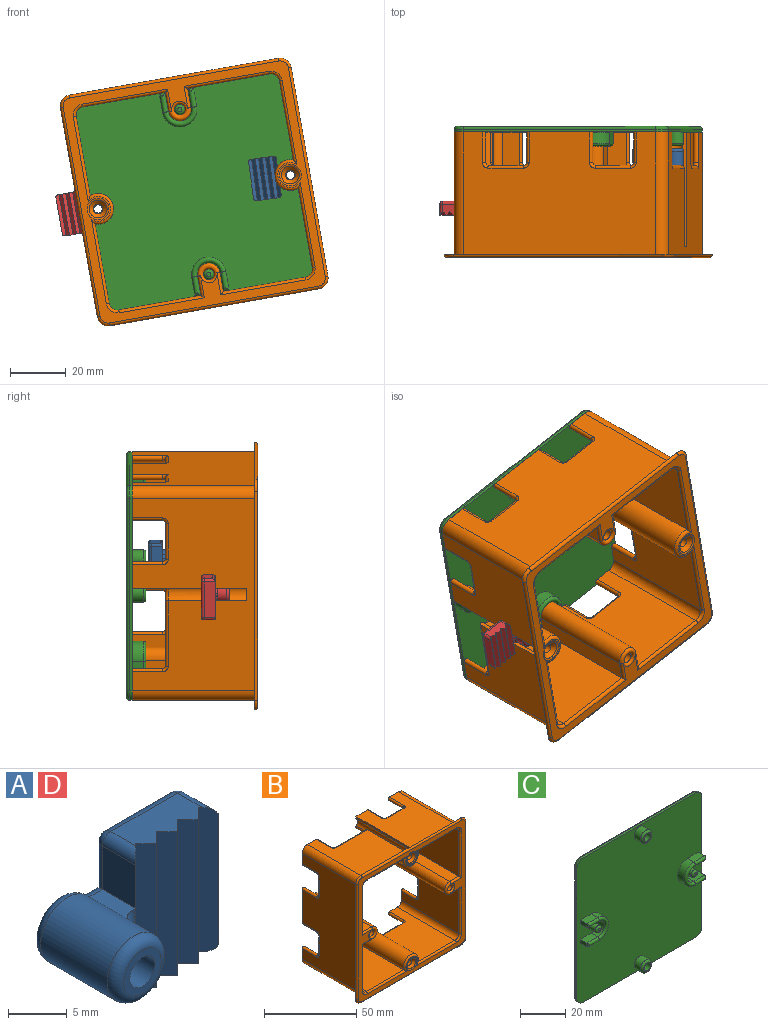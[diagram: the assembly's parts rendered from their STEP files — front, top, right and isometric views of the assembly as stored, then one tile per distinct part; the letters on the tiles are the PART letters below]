
ASSEMBLY  parts=4 mates=3
PART A: 42 faces, bbox 17.9x10.2x15.2 mm
  f0: plane 1.35x0.45mm, normal (0,-1,0), area 0.2mm2, adj f3,f18,f39
  f1: plane 8x4mm, normal (0,0,-1), area 26.8mm2, adj f12,f13,f14,f15,f16,f17,f18,f19
  f2: plane 4.5x4mm, normal (-1,0,0), area 18mm2, adj f3,f18,f27,f32
  f3: plane 5.17x1.81mm, normal (0,0,1), area 6.8mm2, adj f0,f2,f10,f34,f39
  f4: plane 5.17x1.81mm, normal (0,0,-1), area 6.8mm2, adj f5,f8,f10,f36,f41
  f5: plane 4.5x4mm, normal (-1,0,0), area 18mm2, adj f4,f18,f28,f33
  f6: plane 13x4mm, normal (1,0,0), area 52mm2, adj f13,f21,f22,f23
  f7: plane 8x4mm, normal (0,0,1), area 26.7mm2, adj f12,f13,f14,f15,f16,f17,f18,f19
  f8: plane 1.35x0.45mm, normal (0,-1,0), area 0.2mm2, adj f4,f18,f41
  f9: plane 13x10.91mm, normal (0,1,0), area 109.5mm2, adj f23,f26,f29,f32,f33,f34,f36,f37
  f10: cylinder r=3.25mm len=8mm, axis (0,1,0), area 141.8mm2, adj f3,f4,f35,f38,f39,f40,f41
  f11: plane 4.5x4.5mm, normal (0,-1,0), area 8.8mm2, adj f20,f38
  f12: plane 15x1.25mm, normal (0.71,-0.71,0), area 26.5mm2, adj f1,f7,f13,f17
  f13: plane 15x1.25mm, normal (-0.71,-0.71,0), area 25.9mm2, adj f1,f6,f7,f12,f21,f22
  f14: plane 15x1.25mm, normal (0.71,-0.71,0), area 26.5mm2, adj f1,f7,f15,f19
  f15: plane 15x1.25mm, normal (-0.71,-0.71,0), area 26.5mm2, adj f1,f7,f14,f16
  f16: plane 15x1.25mm, normal (0.71,-0.71,0), area 26.5mm2, adj f1,f7,f15,f17
  f17: plane 15x1.25mm, normal (-0.71,-0.71,0), area 26.5mm2, adj f1,f7,f12,f16
  f18: plane 15x1.25mm, normal (0.71,-0.71,0), area 25.9mm2, adj f0,f1,f2,f5,f7,f8,f19,f27
  f19: plane 15x1.25mm, normal (-0.71,-0.71,0), area 26.5mm2, adj f1,f7,f14,f18
  f20: cylinder r=1.5mm len=9mm, axis (0,1,0), area 84.8mm2, adj f11,f37
  f21: cylinder r=1mm len=4mm, axis (0,1,0), area 5.7mm2, adj f6,f7,f13,f24
  f22: cylinder r=1mm len=4mm, axis (0,-1,0), area 5.7mm2, adj f1,f6,f13,f25
  f23: cylinder r=1mm len=13mm, axis (0,0,1), area 20.4mm2, adj f6,f9,f24,f25
  f24: sphere r=1mm, area 1.6mm2, adj f21,f23,f26
  f25: sphere r=1mm, area 1.6mm2, adj f22,f23,f29
  f26: cylinder r=1mm len=8mm, axis (-1,0,0), area 12.6mm2, adj f7,f9,f24,f30
  f27: cylinder r=1mm len=4mm, axis (0,-1,0), area 5.7mm2, adj f2,f7,f18,f30
  f28: cylinder r=1mm len=4mm, axis (0,1,0), area 5.7mm2, adj f1,f5,f18,f31
  f29: cylinder r=1mm len=8mm, axis (1,0,0), area 12.6mm2, adj f1,f9,f25,f31
  f30: sphere r=1mm, area 1.6mm2, adj f26,f27,f32
  f31: sphere r=1mm, area 1.6mm2, adj f28,f29,f33
  f32: cylinder r=1mm len=5.5mm, axis (0,0,-1), area 7.6mm2, adj f2,f9,f30,f34
  f33: cylinder r=1mm len=5.5mm, axis (0,0,-1), area 7.6mm2, adj f5,f9,f31,f36
  f34: cylinder r=1mm len=3.11mm, axis (-1,0,0), area 3.4mm2, adj f3,f9,f32,f35,f37
  f35: torus R=2.25mm, axis (0,-1,0), area 21.5mm2, adj f10,f34,f36,f37
  f36: cylinder r=1mm len=3.11mm, axis (1,0,0), area 3.4mm2, adj f4,f9,f33,f35,f37
  f37: torus R=2.5mm, axis (0,-1,0), area 16.7mm2, adj f9,f20,f34,f35,f36
  f38: torus R=2.25mm, axis (0,-1,0), area 28.5mm2, adj f10,f11
  f39: torus R=4.25mm, axis (0,-1,0), area 2.4mm2, adj f0,f3,f10,f40
  f40: bspline ~1.97x1.08mm, area 1.7mm2, adj f10,f18,f39,f41
  f41: torus R=4.25mm, axis (0,-1,0), area 2.4mm2, adj f4,f8,f10,f40
PART B: 126 faces, bbox 84.8x45.1x84.8 mm
  f0: plane 9.8x8.16mm, normal (0,1,0), area 31.6mm2, adj f2,f11,f16,f23,f27,f88,f116
  f1: plane 9.8x8.16mm, normal (0,1,0), area 31.6mm2, adj f32,f34,f38,f39,f42,f95,f106
  f2: plane 70x44mm, normal (0,0,1), area 2345.8mm2, adj f0,f3,f6,f7,f15,f20,f21,f23
  f3: cylinder r=4mm len=44mm, axis (0,1,0), area 276.5mm2, adj f2,f4,f7,f20
  f4: plane 70x44mm, normal (-1,0,0), area 2641.4mm2, adj f3,f7,f14,f20,f33,f35,f101,f102
  f5: plane 82x82mm, normal (0,-1,0), area 1038.8mm2, adj f52,f53,f54,f55,f56,f57,f58,f59
  f6: plane 29.05x1.42mm, normal (1,0,0), area 36.6mm2, adj f2,f15,f16,f84,f85
  f7: plane 12x12mm, normal (0,1,0), area 41.6mm2, adj f2,f3,f4,f8,f9,f10,f82,f125
  f8: plane 44x30mm, normal (1,0,0), area 1100.7mm2, adj f7,f9,f13,f14,f64,f121,f122,f123
  f9: cylinder r=3mm len=44mm, axis (0,1,0), area 207.3mm2, adj f7,f8,f10,f62
  f10: plane 44x28.88mm, normal (0,0,-1), area 974mm2, adj f7,f9,f11,f60,f82,f83,f84
  f11: cylinder r=5.5mm len=44mm, axis (0,1,0), area 746.3mm2, adj f0,f10,f27,f61,f85,f86,f88
  f12: cylinder r=4mm len=44mm, axis (0,1,0), area 552.9mm2, adj f13,f14,f40,f66
  f13: plane 44x7mm, normal (0,0,1), area 308mm2, adj f8,f12,f14,f67
  f14: plane 24x13mm, normal (0,1,0), area 115.7mm2, adj f4,f8,f12,f13,f17,f36,f40,f105
  f15: plane 7.5x7mm, normal (0,1,0), area 32.1mm2, adj f2,f6,f16,f18,f23
  f16: cylinder r=3.5mm len=41mm, axis (0,1,0), area 559.4mm2, adj f0,f6,f15,f23,f85,f87,f88
  f17: cylinder r=2mm len=44mm, axis (0,1,0), area 552.9mm2, adj f14,f66
  f18: cylinder r=1.75mm len=3.5mm, axis (0,-1,0), area 24.7mm2, adj f15,f19
  f19: cone r=1.75mm half-angle=45deg, axis (0,-1,0), area 32.1mm2, adj f18,f81
  f20: plane 84x84mm, normal (0,1,0), area 972mm2, adj f2,f3,f4,f21,f22,f32,f33,f45
  f21: cylinder r=4mm len=44mm, axis (0,1,0), area 276.5mm2, adj f2,f20,f22,f24
  f22: plane 70x44mm, normal (1,0,0), area 2641.4mm2, adj f20,f21,f24,f30,f45,f47,f96,f97
  f23: plane 41x1.28mm, normal (-1,0,0), area 52.4mm2, adj f0,f2,f15,f16
  f24: plane 12x12mm, normal (0,1,0), area 41.6mm2, adj f2,f21,f22,f25,f26,f27,f111,f120
  f25: plane 44x30mm, normal (-1,0,0), area 1100.7mm2, adj f24,f26,f29,f30,f68,f111,f112,f113
  f26: cylinder r=3mm len=44mm, axis (0,1,0), area 207.3mm2, adj f24,f25,f27,f65
  f27: plane 44x28.88mm, normal (0,0,-1), area 1051.3mm2, adj f0,f11,f24,f26,f63,f116,f117,f118
  f28: cylinder r=4mm len=44mm, axis (0,1,0), area 552.9mm2, adj f29,f30,f51,f70
  f29: plane 44x7mm, normal (0,0,1), area 308mm2, adj f25,f28,f30,f69
  f30: plane 24x13mm, normal (0,1,0), area 115.7mm2, adj f22,f25,f28,f29,f31,f48,f51,f100
  f31: cylinder r=2mm len=44mm, axis (0,1,0), area 552.9mm2, adj f30,f70
  f32: plane 70x44mm, normal (0,0,-1), area 2345.8mm2, adj f1,f20,f33,f34,f35,f41,f45,f46
  f33: cylinder r=4mm len=44mm, axis (0,1,0), area 276.5mm2, adj f4,f20,f32,f35
  f34: plane 41x1.28mm, normal (1,0,0), area 52.4mm2, adj f1,f32,f41,f42
  f35: plane 12x12mm, normal (0,1,0), area 41.6mm2, adj f4,f32,f33,f36,f37,f38,f101,f110
  f36: plane 44x30mm, normal (1,0,0), area 1100.7mm2, adj f14,f35,f37,f40,f72,f101,f102,f103
  f37: cylinder r=3mm len=44mm, axis (0,1,0), area 207.3mm2, adj f35,f36,f38,f74
  f38: plane 44x28.88mm, normal (0,0,1), area 1051.3mm2, adj f1,f35,f37,f39,f76,f106,f107,f108
  f39: cylinder r=5.5mm len=44mm, axis (0,1,0), area 746.3mm2, adj f1,f38,f50,f78,f92,f93,f95
  f40: plane 44x7mm, normal (0,0,-1), area 308mm2, adj f12,f14,f36,f71
  f41: plane 7.5x7mm, normal (0,1,0), area 32.1mm2, adj f32,f34,f42,f43,f46
  f42: cylinder r=3.5mm len=41mm, axis (0,1,0), area 559.4mm2, adj f1,f34,f41,f46,f92,f94,f95
  f43: cylinder r=1.75mm len=3.5mm, axis (0,-1,0), area 24.7mm2, adj f41,f44
  f44: cone r=1.75mm half-angle=45deg, axis (0,-1,0), area 32.1mm2, adj f43,f80
  f45: cylinder r=4mm len=44mm, axis (0,1,0), area 276.5mm2, adj f20,f22,f32,f47
  f46: plane 29.05x1.42mm, normal (-1,0,0), area 36.6mm2, adj f32,f41,f42,f91,f92
  f47: plane 12x12mm, normal (0,1,0), area 41.6mm2, adj f22,f32,f45,f48,f49,f50,f89,f96
  f48: plane 44x30mm, normal (-1,0,0), area 1100.7mm2, adj f30,f47,f49,f51,f75,f96,f97,f98
  f49: cylinder r=3mm len=44mm, axis (0,1,0), area 207.3mm2, adj f47,f48,f50,f77
  f50: plane 44x28.88mm, normal (0,0,1), area 974mm2, adj f39,f47,f49,f79,f89,f90,f91
  f51: plane 44x7mm, normal (0,0,-1), area 308mm2, adj f28,f30,f48,f73
  f52: torus R=3mm, axis (0,-1,0), area 9mm2, adj f5,f20,f53,f54
  f53: cylinder r=1mm len=76mm, axis (0,0,-1), area 119.4mm2, adj f5,f20,f52,f55
  f54: cylinder r=1mm len=76mm, axis (-1,0,0), area 119.4mm2, adj f5,f20,f52,f56
  f55: torus R=3mm, axis (0,-1,0), area 9mm2, adj f5,f20,f53,f57
  f56: torus R=3mm, axis (0,-1,0), area 9mm2, adj f5,f20,f54,f58
  f57: cylinder r=1mm len=76mm, axis (-1,0,0), area 119.4mm2, adj f5,f20,f55,f59
  f58: cylinder r=1mm len=76mm, axis (0,0,-1), area 119.4mm2, adj f5,f20,f56,f59
  f59: torus R=3mm, axis (0,-1,0), area 9mm2, adj f5,f20,f57,f58
  f60: cylinder r=1mm len=30.65mm, axis (-1,0,0), area 46.3mm2, adj f5,f10,f61,f62
  f61: torus R=4.5mm, axis (0,-1,0), area 33.1mm2, adj f5,f11,f60,f63
  f62: torus R=4mm, axis (0,-1,0), area 8.3mm2, adj f5,f9,f60,f64
  f63: cylinder r=1mm len=30.65mm, axis (1,0,0), area 46.3mm2, adj f5,f27,f61,f65
  f64: cylinder r=1mm len=31mm, axis (0,0,-1), area 47.9mm2, adj f5,f8,f62,f67
  f65: torus R=4mm, axis (0,-1,0), area 8.3mm2, adj f5,f26,f63,f68
  f66: torus R=3mm, axis (0,-1,0), area 41.3mm2, adj f5,f12,f17,f67,f71
  f67: cylinder r=1mm len=8mm, axis (1,0,0), area 11.8mm2, adj f5,f13,f64,f66
  f68: cylinder r=1mm len=31mm, axis (0,0,-1), area 47.9mm2, adj f5,f25,f65,f69
  f69: cylinder r=1mm len=8mm, axis (-1,0,0), area 11.8mm2, adj f5,f29,f68,f70
  f70: torus R=3mm, axis (0,-1,0), area 41.3mm2, adj f5,f28,f31,f69,f73
  f71: cylinder r=1mm len=8mm, axis (1,0,0), area 11.8mm2, adj f5,f40,f66,f72
  f72: cylinder r=1mm len=31mm, axis (0,0,1), area 47.9mm2, adj f5,f36,f71,f74
  f73: cylinder r=1mm len=8mm, axis (-1,0,0), area 11.8mm2, adj f5,f51,f70,f75
  f74: torus R=4mm, axis (0,-1,0), area 8.3mm2, adj f5,f37,f72,f76
  f75: cylinder r=1mm len=31mm, axis (0,0,1), area 47.9mm2, adj f5,f48,f73,f77
  f76: cylinder r=1mm len=30.65mm, axis (-1,0,0), area 46.3mm2, adj f5,f38,f74,f78
  f77: torus R=4mm, axis (0,-1,0), area 8.3mm2, adj f5,f49,f75,f79
  f78: torus R=4.5mm, axis (0,-1,0), area 33.1mm2, adj f5,f39,f76,f79
  f79: cylinder r=1mm len=30.65mm, axis (1,0,0), area 46.3mm2, adj f5,f50,f77,f78
  f80: torus R=3.91mm, axis (0,-1,0), area 17.5mm2, adj f5,f44
  f81: torus R=3.91mm, axis (0,-1,0), area 17.5mm2, adj f5,f19
  f82: cylinder r=1mm len=11mm, axis (0,-1,0), area 34.6mm2, adj f2,f7,f10,f83
  f83: torus R=2mm, axis (0,0,1), area 6.7mm2, adj f2,f10,f82,f84
  f84: cylinder r=1mm len=23.8mm, axis (1,0,0), area 70.9mm2, adj f2,f6,f10,f83,f85
  f85: torus R=4.5mm, axis (0,-1,0), area 35.5mm2, adj f6,f11,f16,f84,f86,f87
  f86: bspline ~2.95x2.44mm, area 4.9mm2, adj f11,f85,f87,f88
  f87: bspline ~2.37x1.95mm, area 2.6mm2, adj f16,f85,f86,f88
  f88: cylinder r=1mm len=11mm, axis (0,1,0), area 34.6mm2, adj f0,f11,f16,f86,f87
  f89: cylinder r=1mm len=11mm, axis (0,-1,0), area 34.6mm2, adj f32,f47,f50,f90
  f90: torus R=2mm, axis (0,0,-1), area 6.7mm2, adj f32,f50,f89,f91
  f91: cylinder r=1mm len=23.8mm, axis (-1,0,0), area 70.9mm2, adj f32,f46,f50,f90,f92
  f92: torus R=4.5mm, axis (0,-1,0), area 35.5mm2, adj f39,f42,f46,f91,f93,f94
  f93: bspline ~2.95x2.44mm, area 4.9mm2, adj f39,f92,f94,f95
  f94: bspline ~2.37x1.95mm, area 2.6mm2, adj f42,f92,f93,f95
  f95: cylinder r=1mm len=11mm, axis (0,1,0), area 34.6mm2, adj f1,f39,f42,f93,f94
  f96: cylinder r=1mm len=11mm, axis (0,-1,0), area 34.6mm2, adj f22,f47,f48,f97
  f97: torus R=2mm, axis (-1,0,0), area 6.7mm2, adj f22,f48,f96,f98
  f98: cylinder r=1mm len=13mm, axis (0,0,-1), area 40.8mm2, adj f22,f48,f97,f99
  f99: torus R=2mm, axis (-1,0,0), area 6.7mm2, adj f22,f48,f98,f100
  f100: cylinder r=1mm len=11mm, axis (0,1,0), area 34.6mm2, adj f22,f30,f48,f99
  f101: cylinder r=1mm len=11mm, axis (0,-1,0), area 34.6mm2, adj f4,f35,f36,f102
  f102: torus R=2mm, axis (1,0,0), area 6.7mm2, adj f4,f36,f101,f103
  f103: cylinder r=1mm len=13mm, axis (0,0,-1), area 40.8mm2, adj f4,f36,f102,f104
  f104: torus R=2mm, axis (1,0,0), area 6.7mm2, adj f4,f36,f103,f105
  f105: cylinder r=1mm len=11mm, axis (0,1,0), area 34.6mm2, adj f4,f14,f36,f104
  f106: cylinder r=1mm len=11mm, axis (0,1,0), area 34.6mm2, adj f1,f32,f38,f107
  f107: torus R=2mm, axis (0,0,-1), area 6.7mm2, adj f32,f38,f106,f108
  f108: cylinder r=1mm len=13mm, axis (1,0,0), area 40.8mm2, adj f32,f38,f107,f109
  f109: torus R=2mm, axis (0,0,-1), area 6.7mm2, adj f32,f38,f108,f110
  f110: cylinder r=1mm len=11mm, axis (0,-1,0), area 34.6mm2, adj f32,f35,f38,f109
  f111: cylinder r=1mm len=11mm, axis (0,-1,0), area 34.6mm2, adj f22,f24,f25,f112
  f112: torus R=2mm, axis (-1,0,0), area 6.7mm2, adj f22,f25,f111,f113
  f113: cylinder r=1mm len=13mm, axis (0,0,1), area 40.8mm2, adj f22,f25,f112,f114
  f114: torus R=2mm, axis (-1,0,0), area 6.7mm2, adj f22,f25,f113,f115
  f115: cylinder r=1mm len=11mm, axis (0,1,0), area 34.6mm2, adj f22,f25,f30,f114
  f116: cylinder r=1mm len=11mm, axis (0,1,0), area 34.6mm2, adj f0,f2,f27,f117
  f117: torus R=2mm, axis (0,0,1), area 6.7mm2, adj f2,f27,f116,f118
  f118: cylinder r=1mm len=13mm, axis (-1,0,0), area 40.8mm2, adj f2,f27,f117,f119
  f119: torus R=2mm, axis (0,0,1), area 6.7mm2, adj f2,f27,f118,f120
  f120: cylinder r=1mm len=11mm, axis (0,-1,0), area 34.6mm2, adj f2,f24,f27,f119
  f121: cylinder r=1mm len=11mm, axis (0,1,0), area 34.6mm2, adj f4,f8,f14,f122
  f122: torus R=2mm, axis (1,0,0), area 6.7mm2, adj f4,f8,f121,f123
  f123: cylinder r=1mm len=13mm, axis (0,0,1), area 40.8mm2, adj f4,f8,f122,f124
  f124: torus R=2mm, axis (1,0,0), area 6.7mm2, adj f4,f8,f123,f125
  f125: cylinder r=1mm len=11mm, axis (0,-1,0), area 34.6mm2, adj f4,f7,f8,f124
PART C: 60 faces, bbox 78.7x7x78.7 mm
  f0: plane 78x78mm, normal (0,-1,0), area 5861.7mm2, adj f1,f2,f3,f5,f7,f8,f9,f10
  f1: plane 70x1mm, normal (0,0,1), area 70mm2, adj f0,f2,f13,f52
  f2: cylinder r=4mm len=4mm, axis (0,1,0), area 6.3mm2, adj f0,f1,f3,f54
  f3: plane 70x1mm, normal (-1,0,0), area 70mm2, adj f0,f2,f25,f56
  f4: plane 76x76mm, normal (0,1,0), area 5711.7mm2, adj f50,f51,f52,f53,f54,f55,f56,f57
  f5: cylinder r=3.3mm len=6.6mm, axis (0,1,0), area 82.9mm2, adj f0,f48
  f6: plane 4.6x4.6mm, normal (0,-1,0), area 4.1mm2, adj f12,f48
  f7: plane 6.8x4mm, normal (0,0,-1), area 27.2mm2, adj f0,f8,f11,f38
  f8: cylinder r=4.2mm len=8.4mm, axis (0,1,0), area 52.8mm2, adj f0,f7,f28,f39
  f9: cylinder r=6.2mm len=12.4mm, axis (0,1,0), area 77.9mm2, adj f0,f10,f29,f39
  f10: plane 6.8x4mm, normal (0,0,1), area 27.2mm2, adj f0,f9,f11,f38
  f11: plane 4x2mm, normal (-1,0,0), area 8mm2, adj f0,f7,f10,f37
  f12: cylinder r=2mm len=6mm, axis (0,1,0), area 75.4mm2, adj f6,f59
  f13: cylinder r=4mm len=4mm, axis (0,1,0), area 6.3mm2, adj f0,f1,f14,f50
  f14: plane 70x1mm, normal (1,0,0), area 70mm2, adj f0,f13,f32,f51
  f15: plane 6.8x4mm, normal (0,0,-1), area 27.2mm2, adj f0,f16,f19,f43
  f16: cylinder r=4.2mm len=8.4mm, axis (0,1,0), area 52.8mm2, adj f0,f15,f33,f44
  f17: cylinder r=6.2mm len=12.4mm, axis (0,1,0), area 77.9mm2, adj f0,f18,f34,f44
  f18: plane 6.8x4mm, normal (0,0,1), area 27.2mm2, adj f0,f17,f19,f43
  f19: plane 4x2mm, normal (1,0,0), area 8mm2, adj f0,f15,f18,f42
  f20: cylinder r=1.8mm len=4mm, axis (0,1,0), area 45.2mm2, adj f0,f49
  f21: plane 1.6x1.6mm, normal (0,-1,0), area 2mm2, adj f49
  f22: cylinder r=1.8mm len=4mm, axis (0,1,0), area 45.2mm2, adj f0,f47
  f23: plane 1.6x1.6mm, normal (0,-1,0), area 2mm2, adj f47
  f24: plane 70x1mm, normal (0,0,-1), area 70mm2, adj f0,f25,f32,f55
  f25: cylinder r=4mm len=4mm, axis (0,1,0), area 6.3mm2, adj f0,f3,f24,f57
  f26: cylinder r=3.3mm len=6.6mm, axis (0,1,0), area 82.9mm2, adj f0,f36
  f27: plane 4.6x4.6mm, normal (0,-1,0), area 4.1mm2, adj f31,f36
  f28: plane 6.8x4mm, normal (0,0,1), area 27.2mm2, adj f0,f8,f30,f40
  f29: plane 6.8x4mm, normal (0,0,-1), area 27.2mm2, adj f0,f9,f30,f40
  f30: plane 4x2mm, normal (-1,0,0), area 8mm2, adj f0,f28,f29,f41
  f31: cylinder r=2mm len=6mm, axis (0,1,0), area 75.4mm2, adj f27,f58
  f32: cylinder r=4mm len=4mm, axis (0,1,0), area 6.3mm2, adj f0,f14,f24,f53
  f33: plane 6.8x4mm, normal (0,0,1), area 27.2mm2, adj f0,f16,f35,f45
  f34: plane 6.8x4mm, normal (0,0,-1), area 27.2mm2, adj f0,f17,f35,f45
  f35: plane 4x2mm, normal (1,0,0), area 8mm2, adj f0,f33,f34,f46
  f36: torus R=2.3mm, axis (0,-1,0), area 29mm2, adj f26,f27
  f37: cylinder r=1mm len=2mm, axis (0,0,1), area 2mm2, adj f11,f38
  f38: cylinder r=1mm len=6.8mm, axis (1,0,0), area 20.2mm2, adj f7,f10,f37,f39
  f39: torus R=5.2mm, axis (0,-1,0), area 51.3mm2, adj f8,f9,f38,f40
  f40: cylinder r=1mm len=6.8mm, axis (1,0,0), area 20.2mm2, adj f28,f29,f39,f41
  f41: cylinder r=1mm len=2mm, axis (0,0,-1), area 2mm2, adj f30,f40
  f42: cylinder r=1mm len=2mm, axis (0,0,1), area 2mm2, adj f19,f43
  f43: cylinder r=1mm len=6.8mm, axis (-1,0,0), area 20.2mm2, adj f15,f18,f42,f44
  f44: torus R=5.2mm, axis (0,-1,0), area 51.3mm2, adj f16,f17,f43,f45
  f45: cylinder r=1mm len=6.8mm, axis (-1,0,0), area 20.2mm2, adj f33,f34,f44,f46
  f46: cylinder r=1mm len=2mm, axis (0,0,-1), area 2mm2, adj f35,f45
  f47: torus R=0.8mm, axis (0,-1,0), area 14.2mm2, adj f22,f23
  f48: torus R=2.3mm, axis (0,-1,0), area 29mm2, adj f5,f6
  f49: torus R=0.8mm, axis (0,-1,0), area 14.2mm2, adj f20,f21
  f50: torus R=3mm, axis (0,-1,0), area 9mm2, adj f4,f13,f51,f52
  f51: cylinder r=1mm len=70mm, axis (0,0,-1), area 110mm2, adj f4,f14,f50,f53
  f52: cylinder r=1mm len=70mm, axis (-1,0,0), area 110mm2, adj f1,f4,f50,f54
  f53: torus R=3mm, axis (0,-1,0), area 9mm2, adj f4,f32,f51,f55
  f54: torus R=3mm, axis (0,-1,0), area 9mm2, adj f2,f4,f52,f56
  f55: cylinder r=1mm len=70mm, axis (-1,0,0), area 110mm2, adj f4,f24,f53,f57
  f56: cylinder r=1mm len=70mm, axis (0,0,-1), area 110mm2, adj f3,f4,f54,f57
  f57: torus R=3mm, axis (0,-1,0), area 9mm2, adj f4,f25,f55,f56
  f58: torus R=3mm, axis (0,-1,0), area 23.3mm2, adj f4,f31
  f59: torus R=3mm, axis (0,-1,0), area 23.3mm2, adj f4,f12
PART D: same geometry as A
PLACE A rot(axis=(0,1,0),172.2deg) t=(32.99,57.04,-104.08)mm
PLACE B rot(axis=(0,-1,0),100deg) t=(-1.47,62.91,-110.15)mm
PLACE C rot(axis=(0,-1,0),100deg) t=(-1.46,64.91,-110.24)mm
PLACE D rot(axis=(0,1,0),170deg) t=(-35.94,38.09,-116.23)mm
MATE cylindrical A.f10 <-> B.f39  axis (0,1,0) through (32.99,52.04,-104.08)mm
MATE slider B.f11 <-> D.f10  axis (0,1,0) through (-35.94,42.41,-116.23)mm
MATE fastened C.f5 <-> B.f11  axis (0,-1,0) through (-35.94,62.91,-116.23)mm
